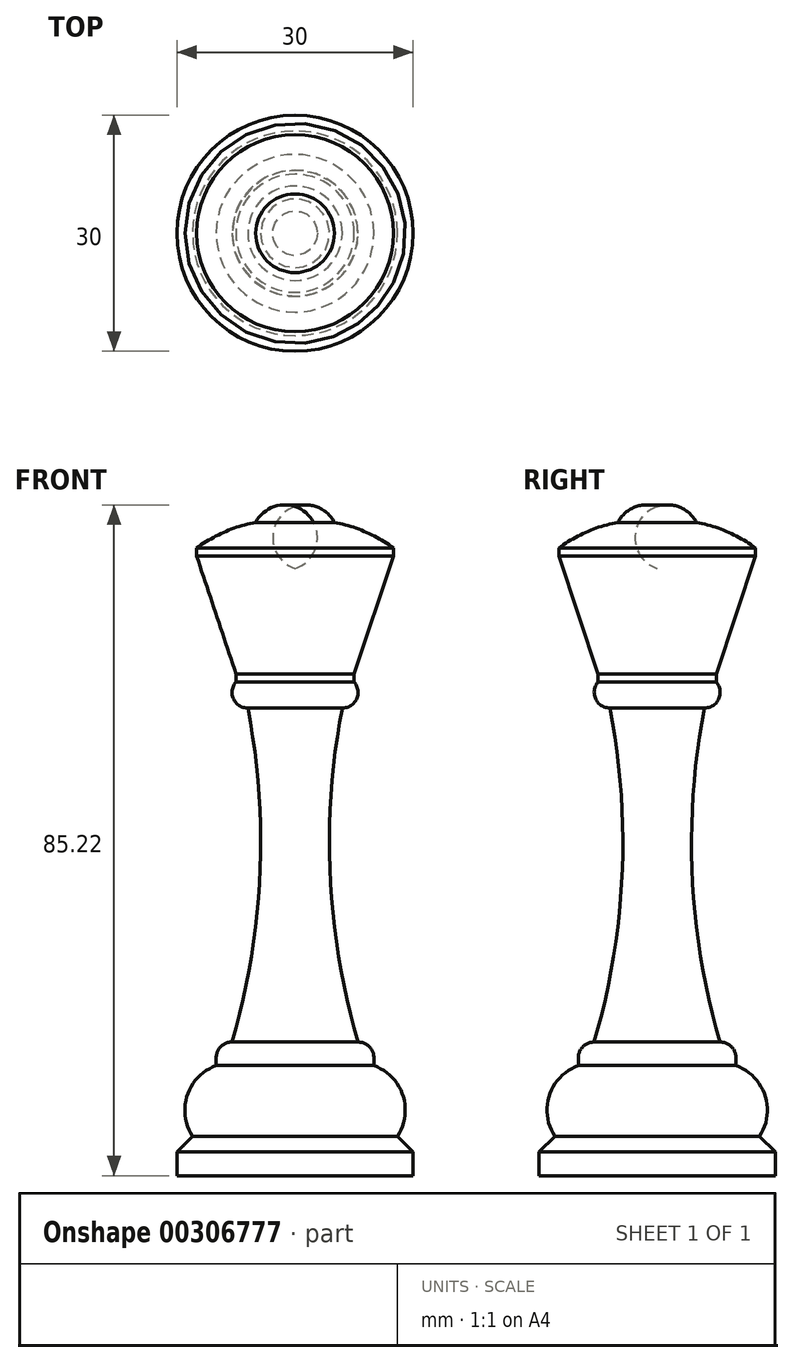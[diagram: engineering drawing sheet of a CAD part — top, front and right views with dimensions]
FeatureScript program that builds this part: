
annotation { "Feature Type Name" : "Feature", "Feature Type Description" : "" }
export const myFeature = defineFeature(function(context is Context, id is Id, definition is map)
    precondition{}
    {
        {
            var Q0;
            Q0=qCreatedBy(makeId("Front.planeOp"),FACE);
            var sketch = newSketch(context, id + "F0", { "sketchPlane" : qUnion([Q0])});
            skArc(sketch, "E0", {"start": v(5, -2) * mm, "mid": v(2.87, -0.08) * mm, "end": v(0, 0) * mm});
            skArc(sketch, "E1", {"start": v(12.5, -5.27) * mm, "mid": v(8.93, -3.21) * mm, "end": v(5, -2) * mm});
            skLineSegment(sketch, "E2", {"start": v(12.5, -5.27) * mm, "end": v(12.5, -6.27) * mm});
            skLineSegment(sketch, "E3", {"start": v(12.5, -6.27) * mm, "end": v(7.5, -21.27) * mm});
            skLineSegment(sketch, "E4", {"start": v(7.5, -21.27) * mm, "end": v(7.5, -22.27) * mm});
            skArc(sketch, "E5", {"start": v(6, -25.6) * mm, "mid": v(7.82, -24.41) * mm, "end": v(7.5, -22.27) * mm});
            skLineSegment(sketch, "E6", {"start": v(10, -70.02) * mm, "end": v(10, -71.02) * mm});
            skArc(sketch, "E7", {"start": v(13, -79.99) * mm, "mid": v(13.7, -74.78) * mm, "end": v(10, -71.02) * mm});
            skLineSegment(sketch, "E8", {"start": v(13, -80) * mm, "end": v(15, -81.99) * mm});
            skLineSegment(sketch, "E9", {"start": v(15, -81.99) * mm, "end": v(15, -85) * mm});
            skLineSegment(sketch, "E10", {"start": v(15, -85) * mm, "end": v(0, -85) * mm});
            skLineSegment(sketch, "E11", {"start": v(0, -85) * mm, "end": v(0, 0) * mm});
            skLineSegment(sketch, "E12", {"start": v(15, -81.99) * mm, "end": v(29.31, -96.3) * mm, "construction": true});
            skLineSegment(sketch, "E13", {"start": v(15, -85) * mm, "end": v(29.85, -85) * mm, "construction": true});
            skArc(sketch, "E14", {"start": v(10, -70.02) * mm, "mid": v(9.42, -68.6) * mm, "end": v(8, -68.02) * mm});
            skArc(sketch, "E15", {"start": v(6, -25.6) * mm, "mid": v(4.46, -46.92) * mm, "end": v(8, -68.02) * mm});
            skSolve(sketch);
        }
        {
            var Q0;
            Q0=makeQuery(id+"F0.imprint","IMPRINT",FACE,{"disambiguationData":[TD([[makeQuery(id+"F0.imprint","IMPRINT",EDGE,{"derivedFrom":sQuery(id+"F0.wireOp",EDGE,"E0")}),1.0]])]});
            var Q1;
            Q1=sQuery(id+"F0.wireOp",EDGE,"E11");
            revolve(context, id + "F1", {"entities" : qUnion([Q0]), "axis" : qUnion([Q1]), "revolveType" : RevolveType.FULL});
        }
    });
